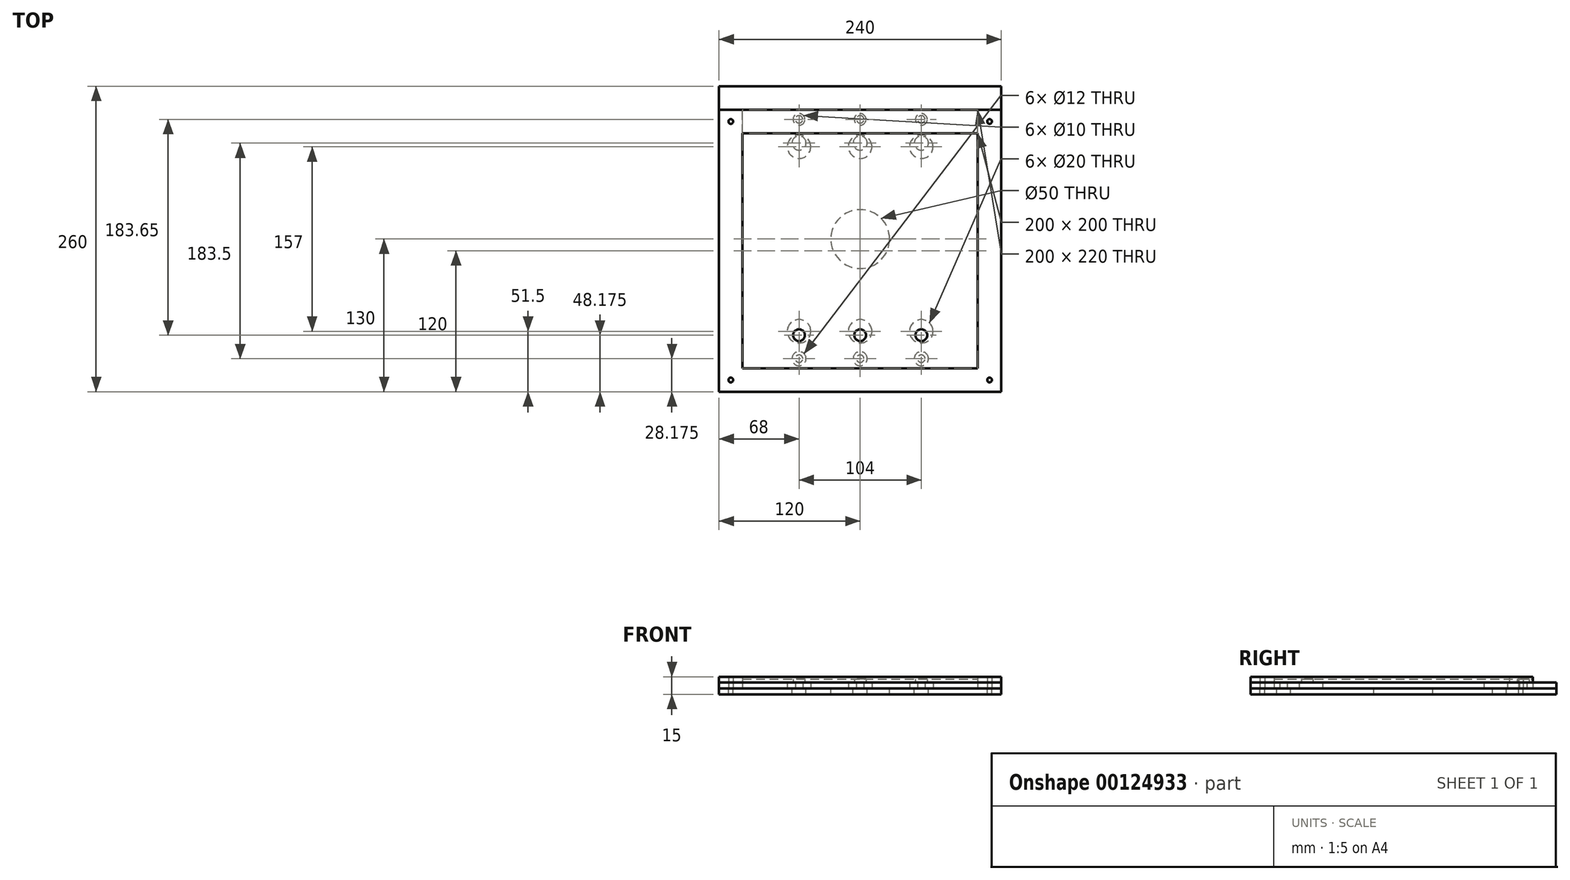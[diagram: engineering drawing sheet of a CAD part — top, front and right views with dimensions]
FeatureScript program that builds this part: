
annotation { "Feature Type Name" : "Feature", "Feature Type Description" : "" }
export const myFeature = defineFeature(function(context is Context, id is Id, definition is map)
    precondition{}
    {
        {
            var Q0;
            Q0=qCreatedBy(makeId("Top.planeOp"),FACE);
            var sketch = newSketch(context, id + "F0", { "sketchPlane" : qUnion([Q0])});
            skLineSegment(sketch, "E0.bottom", {"start": v(0, 0) * mm, "end": v(200, 0) * mm});
            skLineSegment(sketch, "E0.top", {"start": v(0, 220) * mm, "end": v(200, 220) * mm});
            skLineSegment(sketch, "E0.left", {"start": v(0, 0) * mm, "end": v(0, 220) * mm});
            skLineSegment(sketch, "E0.right", {"start": v(200, 0) * mm, "end": v(200, 220) * mm});
            skCircle(sketch, "E1", {"center": v(48, 211.83) * mm, "radius": 3.17 * mm});
            skCircle(sketch, "E2.1.0.0", {"center": v(100, 211.83) * mm, "radius": 3.17 * mm});
            skCircle(sketch, "E2.2.0.0", {"center": v(152, 211.82) * mm, "radius": 3.17 * mm});
            skLineSegment(sketch, "E2.direction1", {"start": v(48, 211.83) * mm, "end": v(100, 211.83) * mm, "construction": true});
            skLineSegment(sketch, "E3", {"start": v(0, 110) * mm, "end": v(200, 110) * mm, "construction": true});
            skCircle(sketch, "E4.MirrorC", {"center": v(48, 8.17) * mm, "radius": 3.17 * mm});
            skCircle(sketch, "E5.MirrorC", {"center": v(100, 8.18) * mm, "radius": 3.17 * mm});
            skCircle(sketch, "E6.MirrorC", {"center": v(152, 8.17) * mm, "radius": 3.17 * mm});
            skLineSegment(sketch, "E7.bottom", {"start": v(21.5, 188.5) * mm, "end": v(178.5, 188.5) * mm, "construction": true});
            skLineSegment(sketch, "E7.top", {"start": v(21.5, 31.5) * mm, "end": v(178.5, 31.5) * mm, "construction": true});
            skLineSegment(sketch, "E7.left", {"start": v(21.5, 188.5) * mm, "end": v(21.5, 31.5) * mm, "construction": true});
            skLineSegment(sketch, "E7.right", {"start": v(178.5, 188.5) * mm, "end": v(178.5, 31.5) * mm, "construction": true});
            skLineSegment(sketch, "E8", {"start": v(48, 211.83) * mm, "end": v(48, 8.17) * mm, "construction": true});
            skLineSegment(sketch, "E9", {"start": v(100, 8.18) * mm, "end": v(100, 211.83) * mm, "construction": true});
            skLineSegment(sketch, "E10", {"start": v(152, 211.82) * mm, "end": v(152, 8.17) * mm, "construction": true});
            skCircle(sketch, "E11", {"center": v(48, 31.5) * mm, "radius": 10 * mm});
            skCircle(sketch, "E12.0.1.0", {"center": v(48, 188.5) * mm, "radius": 10 * mm});
            skCircle(sketch, "E12.1.0.0", {"center": v(100, 31.5) * mm, "radius": 10 * mm});
            skCircle(sketch, "E12.1.1.0", {"center": v(100, 188.5) * mm, "radius": 10 * mm});
            skCircle(sketch, "E12.2.0.0", {"center": v(152, 31.5) * mm, "radius": 10 * mm});
            skCircle(sketch, "E12.2.1.0", {"center": v(152, 188.5) * mm, "radius": 10 * mm});
            skLineSegment(sketch, "E12.direction1", {"start": v(48, 31.5) * mm, "end": v(100, 31.5) * mm, "construction": true});
            skLineSegment(sketch, "E12.direction2", {"start": v(48, 31.5) * mm, "end": v(48, 188.5) * mm, "construction": true});
            skSolve(sketch);
        }
        {
            var Q0;
            Q0=makeQuery(id+"F0.imprint","IMPRINT",FACE,{"disambiguationData":[TD([[makeQuery(id+"F0.imprint","IMPRINT",EDGE,{"derivedFrom":sQuery(id+"F0.wireOp",EDGE,"E0.bottom")}),1.0]])]});
            extrude(context, id + "F1", {"entities" : qUnion([Q0]), "depth" : 5 * mm});
        }
        {
            var Q0;
            Q0=makeQuery(id+"F1.opExtrude","CAP_FACE",FACE,{"disambiguationData":[OSD([sQuery(id+"F0.wireOp",EDGE,"E0.bottom"),sQuery(id+"F0.wireOp",EDGE,"E0.top"),sQuery(id+"F0.wireOp",EDGE,"E0.left"),sQuery(id+"F0.wireOp",EDGE,"E0.right"),sQuery(id+"F0.wireOp",EDGE,"E1"),sQuery(id+"F0.wireOp",EDGE,"E2.1.0.0"),sQuery(id+"F0.wireOp",EDGE,"E2.2.0.0"),sQuery(id+"F0.wireOp",EDGE,"E4.MirrorC"),sQuery(id+"F0.wireOp",EDGE,"E5.MirrorC"),sQuery(id+"F0.wireOp",EDGE,"E6.MirrorC")])],"isStart":false});
            var sketch = newSketch(context, id + "F2", { "sketchPlane" : qUnion([Q0])});
            skLineSegment(sketch, "E13.bottom", {"start": v(0, 0) * mm, "end": v(200, 0) * mm});
            skLineSegment(sketch, "E13.top", {"start": v(0, 220) * mm, "end": v(200, 220) * mm});
            skLineSegment(sketch, "E13.right", {"start": v(200, 0) * mm, "end": v(200, 220) * mm});
            skCircle(sketch, "E14", {"center": v(48, 211.83) * mm, "radius": 5 * mm});
            skCircle(sketch, "E15.0.1.0", {"center": v(48, 28.18) * mm, "radius": 5 * mm});
            skCircle(sketch, "E15.1.0.0", {"center": v(100, 211.83) * mm, "radius": 5 * mm});
            skCircle(sketch, "E15.1.1.0", {"center": v(100, 28.18) * mm, "radius": 5 * mm});
            skCircle(sketch, "E15.2.0.0", {"center": v(152, 211.83) * mm, "radius": 5 * mm});
            skCircle(sketch, "E15.2.1.0", {"center": v(152, 28.18) * mm, "radius": 5 * mm});
            skLineSegment(sketch, "E15.direction1", {"start": v(48, 211.83) * mm, "end": v(100, 211.83) * mm, "construction": true});
            skLineSegment(sketch, "E15.direction2", {"start": v(48, 211.83) * mm, "end": v(48, 28.18) * mm, "construction": true});
            skLineSegment(sketch, "E16", {"start": v(0, 220) * mm, "end": v(0, 0) * mm});
            skSolve(sketch);
        }
        {
            var Q0;
            Q0 = qSketchRegion(id + "F2", true);
            extrude(context, id + "F3", {"entities" : qUnion([Q0]), "depth" : 3 * mm});
        }
        {
            var Q0;
            Q0=makeQuery(id+"F1.opExtrude","CAP_FACE",FACE,{"disambiguationData":[OSD([sQuery(id+"F0.wireOp",EDGE,"E0.bottom"),sQuery(id+"F0.wireOp",EDGE,"E0.top"),sQuery(id+"F0.wireOp",EDGE,"E0.left"),sQuery(id+"F0.wireOp",EDGE,"E0.right"),sQuery(id+"F0.wireOp",EDGE,"E1"),sQuery(id+"F0.wireOp",EDGE,"E2.1.0.0"),sQuery(id+"F0.wireOp",EDGE,"E2.2.0.0"),sQuery(id+"F0.wireOp",EDGE,"E4.MirrorC"),sQuery(id+"F0.wireOp",EDGE,"E5.MirrorC"),sQuery(id+"F0.wireOp",EDGE,"E6.MirrorC")])],"isStart":true});
            var sketch = newSketch(context, id + "F4", { "sketchPlane" : qUnion([Q0])});
            skLineSegment(sketch, "E17.bottom", {"start": v(0, 0) * mm, "end": v(200, 0) * mm, "construction": true});
            skLineSegment(sketch, "E17.top", {"start": v(0, -220) * mm, "end": v(200, -220) * mm, "construction": true});
            skLineSegment(sketch, "E17.left", {"start": v(0, 0) * mm, "end": v(0, -220) * mm, "construction": true});
            skLineSegment(sketch, "E17.right", {"start": v(200, 0) * mm, "end": v(200, -220) * mm, "construction": true});
            skLineSegment(sketch, "E18.0", {"start": v(-20, 20) * mm, "end": v(220, 20) * mm});
            skLineSegment(sketch, "E18.1", {"start": v(-20, 20) * mm, "end": v(-20, -240) * mm});
            skLineSegment(sketch, "E18.2", {"start": v(-20, -240) * mm, "end": v(220, -240) * mm});
            skLineSegment(sketch, "E18.3", {"start": v(220, 20) * mm, "end": v(220, -240) * mm});
            skCircle(sketch, "E19", {"center": v(48, -8.17) * mm, "radius": 6 * mm});
            skCircle(sketch, "E20.0.1.0", {"center": v(48, -191.67) * mm, "radius": 6 * mm});
            skCircle(sketch, "E20.1.0.0", {"center": v(100, -8.17) * mm, "radius": 6 * mm});
            skCircle(sketch, "E20.1.1.0", {"center": v(100, -191.67) * mm, "radius": 6 * mm});
            skCircle(sketch, "E20.2.0.0", {"center": v(152, -8.17) * mm, "radius": 6 * mm});
            skCircle(sketch, "E20.2.1.0", {"center": v(152, -191.67) * mm, "radius": 6 * mm});
            skLineSegment(sketch, "E20.direction1", {"start": v(48, -8.17) * mm, "end": v(100, -8.17) * mm, "construction": true});
            skLineSegment(sketch, "E20.direction2", {"start": v(48, -8.17) * mm, "end": v(48, -191.67) * mm, "construction": true});
            skCircle(sketch, "E21", {"center": v(100, -110) * mm, "radius": 25 * mm});
            skPoint(sketch, "E21.centerSnap0", {"position": v(0, -110) * mm});
            skCircle(sketch, "E22", {"center": v(-10, 10) * mm, "radius": 2 * mm});
            skCircle(sketch, "E23.0.1.0", {"center": v(-10, -210) * mm, "radius": 2 * mm});
            skCircle(sketch, "E23.1.0.0", {"center": v(210, 10) * mm, "radius": 2 * mm});
            skCircle(sketch, "E23.1.1.0", {"center": v(210, -210) * mm, "radius": 2 * mm});
            skLineSegment(sketch, "E23.direction1", {"start": v(-10, 10) * mm, "end": v(210, 10) * mm, "construction": true});
            skLineSegment(sketch, "E23.direction2", {"start": v(-10, 10) * mm, "end": v(-10, -210) * mm, "construction": true});
            skSolve(sketch);
        }
        {
            var Q0;
            Q0 = qSketchRegion(id + "F4", true);
            extrude(context, id + "F5", {"entities" : qUnion([Q0]), "depth" : 5 * mm});
        }
        {
            var Q0;
            Q0=makeQuery(id+"F5.opExtrude","CAP_FACE",FACE,{"disambiguationData":[OSD([sQuery(id+"F4.wireOp",EDGE,"E18.0"),sQuery(id+"F4.wireOp",EDGE,"E18.1"),sQuery(id+"F4.wireOp",EDGE,"E18.2"),sQuery(id+"F4.wireOp",EDGE,"E18.3"),sQuery(id+"F4.wireOp",EDGE,"E19"),sQuery(id+"F4.wireOp",EDGE,"E20.0.1.0"),sQuery(id+"F4.wireOp",EDGE,"E20.1.0.0"),sQuery(id+"F4.wireOp",EDGE,"E20.1.1.0"),sQuery(id+"F4.wireOp",EDGE,"E20.2.0.0"),sQuery(id+"F4.wireOp",EDGE,"E20.2.1.0"),sQuery(id+"F4.wireOp",EDGE,"E21"),sQuery(id+"F4.wireOp",EDGE,"E22"),sQuery(id+"F4.wireOp",EDGE,"E23.0.1.0"),sQuery(id+"F4.wireOp",EDGE,"E23.1.0.0"),sQuery(id+"F4.wireOp",EDGE,"E23.1.1.0")])],"isStart":true});
            var sketch = newSketch(context, id + "F6", { "sketchPlane" : qUnion([Q0])});
            skLineSegment(sketch, "E24.bottom", {"start": v(-20, 240) * mm, "end": v(220, 240) * mm});
            skLineSegment(sketch, "E24.top", {"start": v(-20, -20) * mm, "end": v(220, -20) * mm});
            skLineSegment(sketch, "E24.left", {"start": v(-20, 240) * mm, "end": v(-20, -20) * mm});
            skLineSegment(sketch, "E24.right", {"start": v(220, 240) * mm, "end": v(220, -20) * mm});
            skLineSegment(sketch, "E25.0", {"start": v(0, 220) * mm, "end": v(200, 220) * mm});
            skLineSegment(sketch, "E25.1", {"start": v(0, 220) * mm, "end": v(0, 0) * mm});
            skLineSegment(sketch, "E25.2", {"start": v(0, 0) * mm, "end": v(200, 0) * mm});
            skLineSegment(sketch, "E25.3", {"start": v(200, 220) * mm, "end": v(200, 0) * mm});
            skCircle(sketch, "E26", {"center": v(-10, 210) * mm, "radius": 2 * mm});
            skCircle(sketch, "E27.0.1.0", {"center": v(-10, -10) * mm, "radius": 2 * mm});
            skCircle(sketch, "E27.1.0.0", {"center": v(210, 210) * mm, "radius": 2 * mm});
            skCircle(sketch, "E27.1.1.0", {"center": v(210, -10) * mm, "radius": 2 * mm});
            skLineSegment(sketch, "E27.direction1", {"start": v(-10, 210) * mm, "end": v(210, 210) * mm, "construction": true});
            skLineSegment(sketch, "E27.direction2", {"start": v(-10, 210) * mm, "end": v(-10, -10) * mm, "construction": true});
            skSolve(sketch);
        }
        {
            var Q0;
            Q0=makeQuery(id+"F6.imprint","IMPRINT",FACE,{"disambiguationData":[TD([[makeQuery(id+"F6.imprint","IMPRINT",EDGE,{"derivedFrom":sQuery(id+"F6.wireOp",EDGE,"E24.bottom")}),-1.0]])]});
            extrude(context, id + "F7", {"entities" : qUnion([Q0]), "depth" : 5 * mm});
        }
        {
            var Q0;
            Q0=makeQuery(id+"F7.opExtrude","CAP_FACE",FACE,{"disambiguationData":[OSD([sQuery(id+"F6.wireOp",EDGE,"E24.bottom"),sQuery(id+"F6.wireOp",EDGE,"E24.top"),sQuery(id+"F6.wireOp",EDGE,"E24.left"),sQuery(id+"F6.wireOp",EDGE,"E24.right"),sQuery(id+"F6.wireOp",EDGE,"E25.0"),sQuery(id+"F6.wireOp",EDGE,"E25.1"),sQuery(id+"F6.wireOp",EDGE,"E25.2"),sQuery(id+"F6.wireOp",EDGE,"E25.3"),sQuery(id+"F6.wireOp",EDGE,"E26"),sQuery(id+"F6.wireOp",EDGE,"E27.0.1.0"),sQuery(id+"F6.wireOp",EDGE,"E27.1.0.0"),sQuery(id+"F6.wireOp",EDGE,"E27.1.1.0")])],"isStart":false});
            var sketch = newSketch(context, id + "F8", { "sketchPlane" : qUnion([Q0])});
            skLineSegment(sketch, "E28.bottom", {"start": v(-20, 220) * mm, "end": v(220, 220) * mm});
            skLineSegment(sketch, "E28.top", {"start": v(-20, -20) * mm, "end": v(220, -20) * mm});
            skLineSegment(sketch, "E28.left", {"start": v(-20, 220) * mm, "end": v(-20, -20) * mm});
            skLineSegment(sketch, "E28.right", {"start": v(220, 220) * mm, "end": v(220, -20) * mm});
            skLineSegment(sketch, "E29.0", {"start": v(0, 200) * mm, "end": v(200, 200) * mm});
            skLineSegment(sketch, "E29.1", {"start": v(0, 200) * mm, "end": v(0, 0) * mm});
            skLineSegment(sketch, "E29.2", {"start": v(0, 0) * mm, "end": v(200, 0) * mm});
            skLineSegment(sketch, "E29.3", {"start": v(200, 200) * mm, "end": v(200, 0) * mm});
            skCircle(sketch, "E30", {"center": v(-10, 210) * mm, "radius": 2 * mm});
            skCircle(sketch, "E31.0.1.0", {"center": v(-10, -10) * mm, "radius": 2 * mm});
            skCircle(sketch, "E31.1.0.0", {"center": v(210, 210) * mm, "radius": 2 * mm});
            skCircle(sketch, "E31.1.1.0", {"center": v(210, -10) * mm, "radius": 2 * mm});
            skLineSegment(sketch, "E31.direction1", {"start": v(-10, 210) * mm, "end": v(210, 210) * mm, "construction": true});
            skLineSegment(sketch, "E31.direction2", {"start": v(-10, 210) * mm, "end": v(-10, -10) * mm, "construction": true});
            skSolve(sketch);
        }
        {
            var Q0;
            Q0 = qSketchRegion(id + "F8", true);
            extrude(context, id + "F9", {"entities" : qUnion([Q0]), "depth" : 5 * mm});
        }
    });
